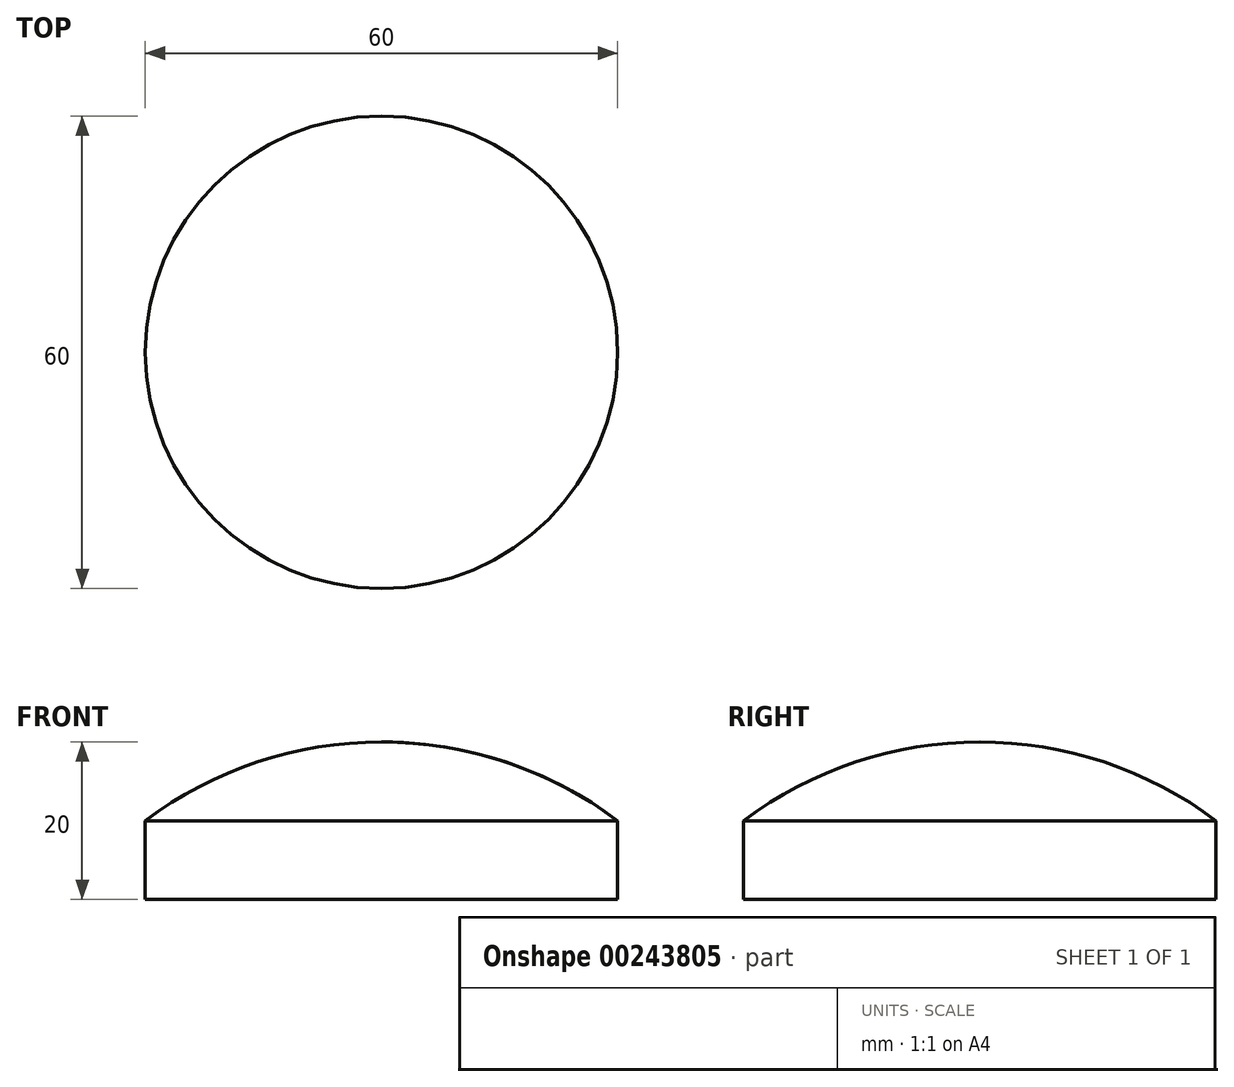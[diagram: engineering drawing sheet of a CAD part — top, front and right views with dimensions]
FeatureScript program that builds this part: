
annotation { "Feature Type Name" : "Feature", "Feature Type Description" : "" }
export const myFeature = defineFeature(function(context is Context, id is Id, definition is map)
    precondition{}
    {
        {
            var Q0;
            Q0=qCreatedBy(makeId("Front.planeOp"),FACE);
            var sketch = newSketch(context, id + "F0", { "sketchPlane" : qUnion([Q0])});
            skLineSegment(sketch, "E0", {"start": v(0, 0) * mm, "end": v(0, 20) * mm});
            skLineSegment(sketch, "E1", {"start": v(0, 0) * mm, "end": v(30, 0) * mm});
            skLineSegment(sketch, "E2", {"start": v(0, -25.13) * mm, "end": v(0, 59.42) * mm, "construction": true});
            skArc(sketch, "E3", {"start": v(30, 10) * mm, "mid": v(15.81, 17.43) * mm, "end": v(0, 20) * mm});
            skLineSegment(sketch, "E4", {"start": v(30, 0) * mm, "end": v(30, 10) * mm});
            skSolve(sketch);
        }
        {
            var Q0;
            Q0 = qSketchRegion(id + "F0", true);
            var Q1;
            Q1=sQuery(id+"F0.wireOp",EDGE,"E2");
            revolve(context, id + "F1", {"entities" : qUnion([Q0]), "axis" : qUnion([Q1]), "revolveType" : RevolveType.FULL});
        }
    });
